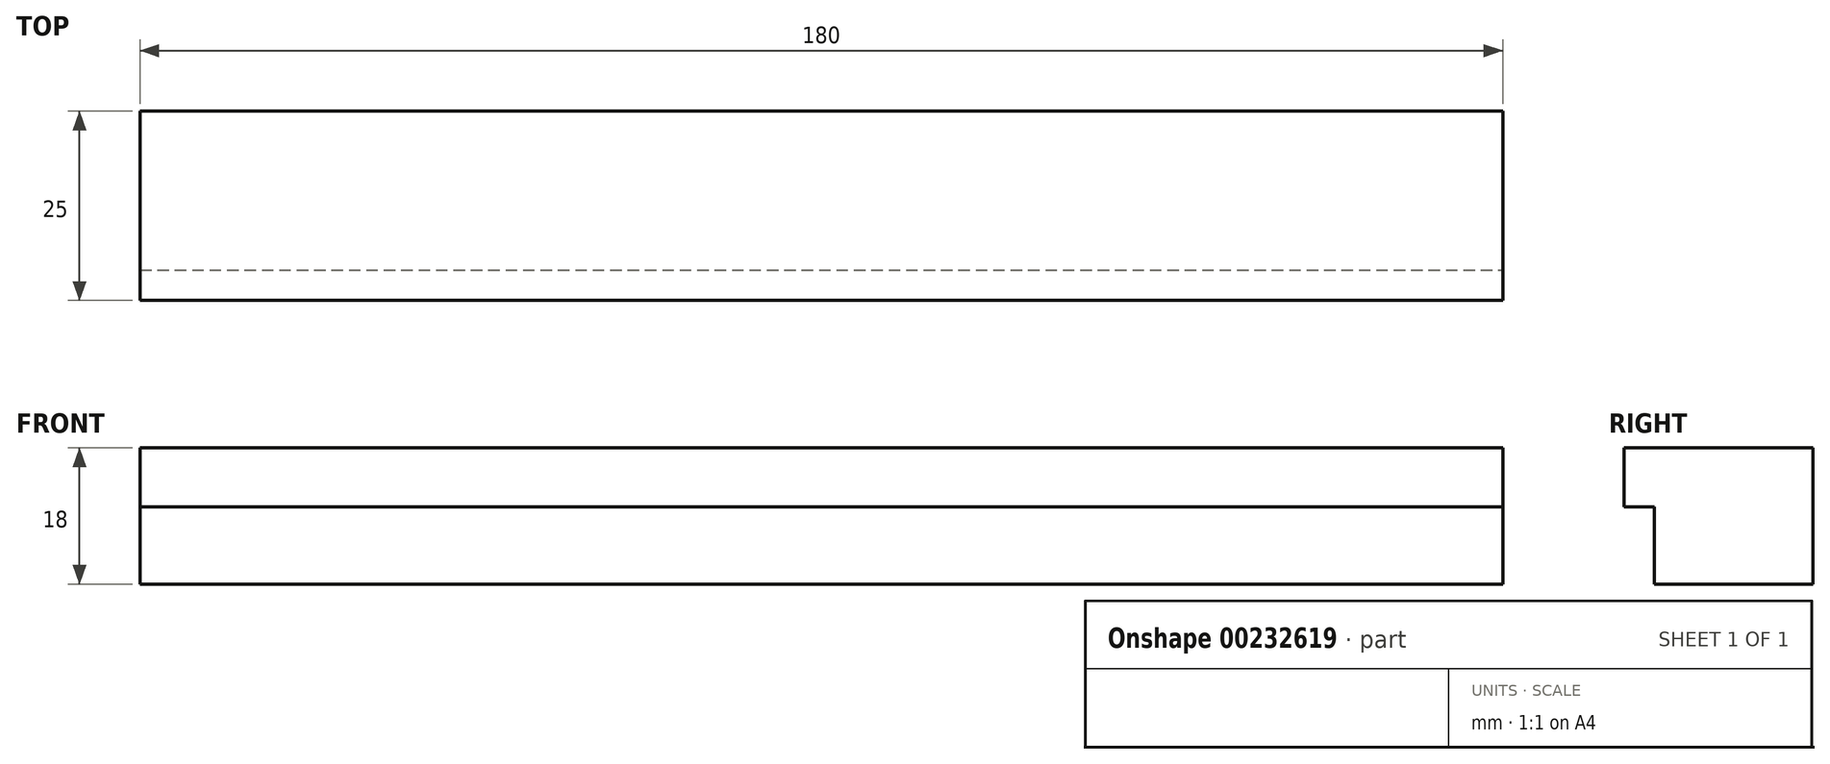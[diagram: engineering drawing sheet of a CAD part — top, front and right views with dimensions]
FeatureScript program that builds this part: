
annotation { "Feature Type Name" : "Feature", "Feature Type Description" : "" }
export const myFeature = defineFeature(function(context is Context, id is Id, definition is map)
    precondition{}
    {
        {
            var Q0;
            Q0=qCreatedBy(makeId("Front.planeOp"),FACE);
            var sketch = newSketch(context, id + "F0", { "sketchPlane" : qUnion([Q0])});
            skLineSegment(sketch, "E0.bottom", {"start": v(0, 0) * mm, "end": v(180, 0) * mm});
            skLineSegment(sketch, "E0.top", {"start": v(0, 18) * mm, "end": v(180, 18) * mm});
            skLineSegment(sketch, "E0.left", {"start": v(0, 0) * mm, "end": v(0, 18) * mm});
            skLineSegment(sketch, "E0.right", {"start": v(180, 0) * mm, "end": v(180, 18) * mm});
            skSolve(sketch);
        }
        {
            var Q0;
            Q0=qSketchRegion(id+"F0",true);
            extrude(context, id + "F1", {"entities" : qUnion([Q0]), "depth" : 25 * mm});
        }
        {
            var Q0;
            Q0=makeQuery(id+"F1.opExtrude","SWEPT_FACE",FACE,{"disambiguationData":[OSD([sQuery(id+"F0.wireOp",EDGE,"E0.right")])]});
            var sketch = newSketch(context, id + "F2", { "sketchPlane" : qUnion([Q0])});
            skLineSegment(sketch, "E1.bottom", {"start": v(-25, 0) * mm, "end": v(-21, 0) * mm});
            skLineSegment(sketch, "E1.top", {"start": v(-25, 10.2) * mm, "end": v(-21, 10.2) * mm});
            skLineSegment(sketch, "E1.left", {"start": v(-25, 0) * mm, "end": v(-25, 10.2) * mm});
            skLineSegment(sketch, "E1.right", {"start": v(-21, 0) * mm, "end": v(-21, 10.2) * mm});
            skSolve(sketch);
        }
        {
            var Q0;
            Q0=qSketchRegion(id+"F2",true);
            extrude(context, id + "F3", {"entities" : qUnion([Q0]), "operationType" : NewBodyOperationType.REMOVE, "endBound" : BoundingType.THROUGH_ALL, "oppositeDirection" : true, "depth" : 25 * mm});
        }
    });
